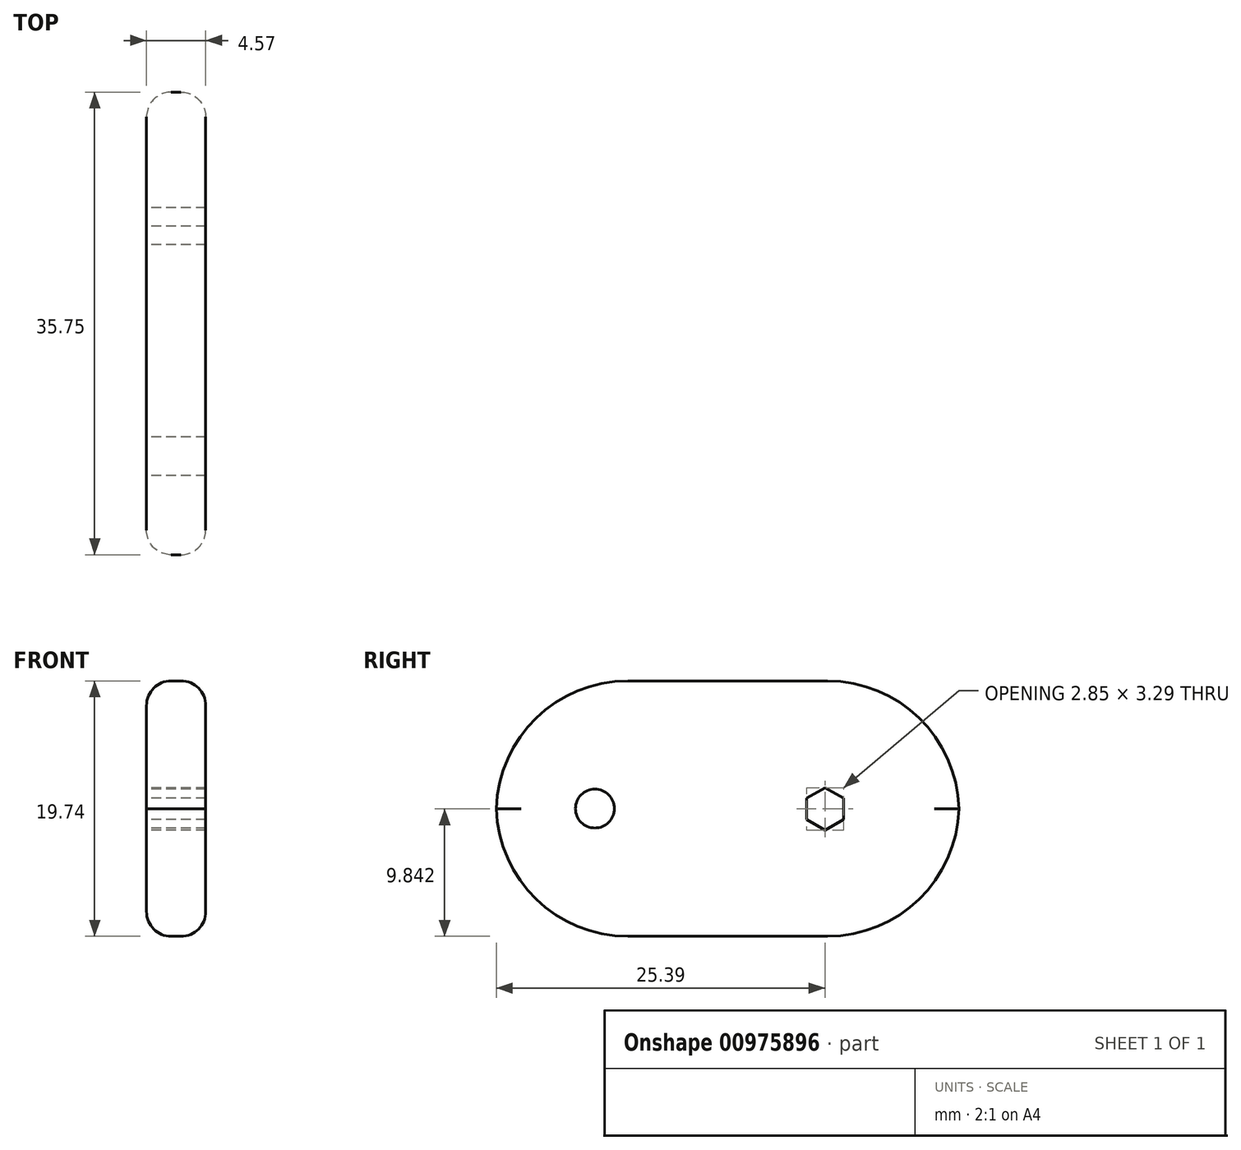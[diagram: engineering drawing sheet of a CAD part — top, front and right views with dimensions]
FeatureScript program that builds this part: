
annotation { "Feature Type Name" : "Feature", "Feature Type Description" : "" }
export const myFeature = defineFeature(function(context is Context, id is Id, definition is map)
    precondition{}
    {
        {
            var Q0;
            Q0=qCreatedBy(makeId("Right.planeOp"),FACE);
            var sketch = newSketch(context, id + "F0", { "sketchPlane" : qUnion([Q0])});
            skCircle(sketch, "E0", {"center": v(0, 0) * mm, "radius": 25.4 * mm});
            skCircle(sketch, "E1", {"center": v(15.88, 0) * mm, "radius": 1.5 * mm});
            skCircle(sketch, "E2", {"center": v(-17.78, 0) * mm, "radius": 1.5 * mm});
            skLineSegment(sketch, "E3.0", {"start": v(1.42, -0.85) * mm, "end": v(0, -1.67) * mm});
            skLineSegment(sketch, "E3.1", {"start": v(0, -1.67) * mm, "end": v(-1.43, -0.85) * mm});
            skLineSegment(sketch, "E3.2", {"start": v(-1.43, -0.85) * mm, "end": v(-1.43, 0.8) * mm});
            skLineSegment(sketch, "E3.3", {"start": v(-1.43, 0.8) * mm, "end": v(0, 1.62) * mm});
            skLineSegment(sketch, "E3.4", {"start": v(0, 1.62) * mm, "end": v(1.43, 0.8) * mm});
            skLineSegment(sketch, "E3.5", {"start": v(1.42, 0.8) * mm, "end": v(1.42, -0.85) * mm});
            skPoint(sketch, "E3.0.midPoint", {"position": v(0.71, -1.26) * mm});
            skLineSegment(sketch, "E4", {"start": v(23.4, 9.87) * mm, "end": v(-23.4, 9.87) * mm});
            skLineSegment(sketch, "E5.MirrorCS", {"start": v(23.4, -9.87) * mm, "end": v(-23.4, -9.87) * mm});
            skLineSegment(sketch, "E6", {"start": v(10.36, 9.87) * mm, "end": v(10.36, -9.87) * mm});
            skSolve(sketch);
        }
        {
            var Q0;
            Q0=makeQuery(id+"F0.imprint","IMPRINT",FACE,{"disambiguationData":[TD([[makeQuery(id+"F0.imprint","IMPRINT",EDGE,{"derivedFrom":sQuery(id+"F0.wireOp",EDGE,"E2")}),-1.0]])]});
            extrude(context, id + "F1", {"entities" : qUnion([Q0]), "depth" : 4.57 * mm, "offsetDistance" : 25.4 * mm});
        }
        {
            var Q0;
            {var subQ0=sQuery(id+"F0.wireOp",EDGE,"E4");var subQ1=sQuery(id+"F0.wireOp",EDGE,"E0");Q0=makeQuery(id+"F1.opExtrude","SWEPT_EDGE",EDGE,{"disambiguationData":[OSD([subQ1,subQ0]),TDD([makeQuery(id+"F0.imprint","INTERSECT",VERTEX,{"disambiguationData":[OD(0.0)],"derivedFrom":[subQ1,subQ0]})])]});}
            var Q1;
            {var subQ0=sQuery(id+"F0.wireOp",EDGE,"E4");var subQ1=sQuery(id+"F0.wireOp",EDGE,"E0");Q1=makeQuery(id+"F1.opExtrude","SWEPT_EDGE",EDGE,{"disambiguationData":[OSD([subQ1,subQ0]),TDD([makeQuery(id+"F0.imprint","INTERSECT",VERTEX,{"disambiguationData":[OD(1.0)],"derivedFrom":[subQ1,subQ0]})])]});}
            var Q2;
            {var subQ0=sQuery(id+"F0.wireOp",EDGE,"E5.MirrorCS");var subQ1=sQuery(id+"F0.wireOp",EDGE,"E0");Q2=makeQuery(id+"F1.opExtrude","SWEPT_EDGE",EDGE,{"disambiguationData":[OSD([subQ1,subQ0]),TDD([makeQuery(id+"F0.imprint","INTERSECT",VERTEX,{"disambiguationData":[OD(1.0)],"derivedFrom":[subQ1,subQ0]})])]});}
            var Q3;
            {var subQ0=sQuery(id+"F0.wireOp",EDGE,"E5.MirrorCS");var subQ1=sQuery(id+"F0.wireOp",EDGE,"E0");Q3=makeQuery(id+"F1.opExtrude","SWEPT_EDGE",EDGE,{"disambiguationData":[OSD([subQ1,subQ0]),TDD([makeQuery(id+"F0.imprint","INTERSECT",VERTEX,{"disambiguationData":[OD(0.0)],"derivedFrom":[subQ1,subQ0]})])]});}
            fillet(context, id + "F2", {"entities" : qUnion([Q0, Q1, Q2, Q3]), "radius" : 10.16 * mm, "tangentPropagation" : true, "allowEdgeOverflow" : false});
        }
        {
            var Q0;
            Q0=makeQuery(id+"F1.opExtrude","SWEPT_EDGE",EDGE,{"disambiguationData":[OSD([sQuery(id+"F0.wireOp",EDGE,"E4"),sQuery(id+"F0.wireOp",EDGE,"E6")])]});
            var Q1;
            Q1=makeQuery(id+"F1.opExtrude","SWEPT_EDGE",EDGE,{"disambiguationData":[OSD([sQuery(id+"F0.wireOp",EDGE,"E5.MirrorCS"),sQuery(id+"F0.wireOp",EDGE,"E6")])]});
            fillet(context, id + "F3", {"entities" : qUnion([Q0, Q1]), "radius" : 10.16 * mm, "tangentPropagation" : true, "allowEdgeOverflow" : false});
        }
        {
            var Q0;
            {var subQ0=sQuery(id+"F0.wireOp",EDGE,"E6");var subQ1=sQuery(id+"F0.wireOp",EDGE,"E4");Q0=makeQuery(id+"F3.opFillet","BLEND_EDGE",EDGE,{"blendedFrom":[makeQuery(id+"F1.opExtrude","SWEPT_EDGE",EDGE,{"disambiguationData":[OSD([subQ1,subQ0])]}),makeQuery(id+"F1.opExtrude","CAP_FACE",FACE,{"disambiguationData":[OSD([sQuery(id+"F0.wireOp",EDGE,"E0"),sQuery(id+"F0.wireOp",EDGE,"E2"),sQuery(id+"F0.wireOp",EDGE,"E3.0"),sQuery(id+"F0.wireOp",EDGE,"E3.1"),sQuery(id+"F0.wireOp",EDGE,"E3.2"),sQuery(id+"F0.wireOp",EDGE,"E3.3"),sQuery(id+"F0.wireOp",EDGE,"E3.4"),sQuery(id+"F0.wireOp",EDGE,"E3.5"),subQ1,sQuery(id+"F0.wireOp",EDGE,"E5.MirrorCS"),subQ0])],"isStart":true})],"blendedInto":[makeQuery(id+"F1.opExtrude","CAP_FACE",FACE,{"disambiguationData":[OSD([sQuery(id+"F0.wireOp",EDGE,"E0"),sQuery(id+"F0.wireOp",EDGE,"E2"),sQuery(id+"F0.wireOp",EDGE,"E3.0"),sQuery(id+"F0.wireOp",EDGE,"E3.1"),sQuery(id+"F0.wireOp",EDGE,"E3.2"),sQuery(id+"F0.wireOp",EDGE,"E3.3"),sQuery(id+"F0.wireOp",EDGE,"E3.4"),sQuery(id+"F0.wireOp",EDGE,"E3.5"),subQ1,sQuery(id+"F0.wireOp",EDGE,"E5.MirrorCS"),subQ0])],"isStart":true})]});}
            var Q1;
            Q1=makeQuery(id+"F1.opExtrude","CAP_EDGE",EDGE,{"disambiguationData":[OSD([sQuery(id+"F0.wireOp",EDGE,"E4")])],"isStart":true});
            var Q2;
            {var subQ0=sQuery(id+"F0.wireOp",EDGE,"E4");var subQ1=sQuery(id+"F0.wireOp",EDGE,"E0");Q2=makeQuery(id+"F2.opFillet","BLEND_EDGE",EDGE,{"blendedFrom":[makeQuery(id+"F1.opExtrude","SWEPT_EDGE",EDGE,{"disambiguationData":[OSD([subQ1,subQ0])]}),makeQuery(id+"F1.opExtrude","CAP_FACE",FACE,{"disambiguationData":[OSD([subQ1,sQuery(id+"F0.wireOp",EDGE,"E2"),sQuery(id+"F0.wireOp",EDGE,"E3.0"),sQuery(id+"F0.wireOp",EDGE,"E3.1"),sQuery(id+"F0.wireOp",EDGE,"E3.2"),sQuery(id+"F0.wireOp",EDGE,"E3.3"),sQuery(id+"F0.wireOp",EDGE,"E3.4"),sQuery(id+"F0.wireOp",EDGE,"E3.5"),subQ0,sQuery(id+"F0.wireOp",EDGE,"E5.MirrorCS"),sQuery(id+"F0.wireOp",EDGE,"E6")])],"isStart":true})],"blendedInto":[makeQuery(id+"F1.opExtrude","CAP_FACE",FACE,{"disambiguationData":[OSD([subQ1,sQuery(id+"F0.wireOp",EDGE,"E2"),sQuery(id+"F0.wireOp",EDGE,"E3.0"),sQuery(id+"F0.wireOp",EDGE,"E3.1"),sQuery(id+"F0.wireOp",EDGE,"E3.2"),sQuery(id+"F0.wireOp",EDGE,"E3.3"),sQuery(id+"F0.wireOp",EDGE,"E3.4"),sQuery(id+"F0.wireOp",EDGE,"E3.5"),subQ0,sQuery(id+"F0.wireOp",EDGE,"E5.MirrorCS"),sQuery(id+"F0.wireOp",EDGE,"E6")])],"isStart":true})]});}
            var Q3;
            {var subQ0=sQuery(id+"F0.wireOp",EDGE,"E5.MirrorCS");var subQ1=sQuery(id+"F0.wireOp",EDGE,"E0");Q3=makeQuery(id+"F2.opFillet","BLEND_EDGE",EDGE,{"blendedFrom":[makeQuery(id+"F1.opExtrude","SWEPT_EDGE",EDGE,{"disambiguationData":[OSD([subQ1,subQ0])]}),makeQuery(id+"F1.opExtrude","CAP_FACE",FACE,{"disambiguationData":[OSD([subQ1,sQuery(id+"F0.wireOp",EDGE,"E2"),sQuery(id+"F0.wireOp",EDGE,"E3.0"),sQuery(id+"F0.wireOp",EDGE,"E3.1"),sQuery(id+"F0.wireOp",EDGE,"E3.2"),sQuery(id+"F0.wireOp",EDGE,"E3.3"),sQuery(id+"F0.wireOp",EDGE,"E3.4"),sQuery(id+"F0.wireOp",EDGE,"E3.5"),sQuery(id+"F0.wireOp",EDGE,"E4"),subQ0,sQuery(id+"F0.wireOp",EDGE,"E6")])],"isStart":true})],"blendedInto":[makeQuery(id+"F1.opExtrude","CAP_FACE",FACE,{"disambiguationData":[OSD([subQ1,sQuery(id+"F0.wireOp",EDGE,"E2"),sQuery(id+"F0.wireOp",EDGE,"E3.0"),sQuery(id+"F0.wireOp",EDGE,"E3.1"),sQuery(id+"F0.wireOp",EDGE,"E3.2"),sQuery(id+"F0.wireOp",EDGE,"E3.3"),sQuery(id+"F0.wireOp",EDGE,"E3.4"),sQuery(id+"F0.wireOp",EDGE,"E3.5"),sQuery(id+"F0.wireOp",EDGE,"E4"),subQ0,sQuery(id+"F0.wireOp",EDGE,"E6")])],"isStart":true})]});}
            var Q4;
            Q4=makeQuery(id+"F1.opExtrude","CAP_EDGE",EDGE,{"disambiguationData":[OSD([sQuery(id+"F0.wireOp",EDGE,"E5.MirrorCS")])],"isStart":true});
            var Q5;
            {var subQ0=sQuery(id+"F0.wireOp",EDGE,"E6");var subQ1=sQuery(id+"F0.wireOp",EDGE,"E5.MirrorCS");Q5=makeQuery(id+"F3.opFillet","BLEND_EDGE",EDGE,{"blendedFrom":[makeQuery(id+"F1.opExtrude","SWEPT_EDGE",EDGE,{"disambiguationData":[OSD([subQ1,subQ0])]}),makeQuery(id+"F1.opExtrude","CAP_FACE",FACE,{"disambiguationData":[OSD([sQuery(id+"F0.wireOp",EDGE,"E0"),sQuery(id+"F0.wireOp",EDGE,"E2"),sQuery(id+"F0.wireOp",EDGE,"E3.0"),sQuery(id+"F0.wireOp",EDGE,"E3.1"),sQuery(id+"F0.wireOp",EDGE,"E3.2"),sQuery(id+"F0.wireOp",EDGE,"E3.3"),sQuery(id+"F0.wireOp",EDGE,"E3.4"),sQuery(id+"F0.wireOp",EDGE,"E3.5"),sQuery(id+"F0.wireOp",EDGE,"E4"),subQ1,subQ0])],"isStart":true})],"blendedInto":[makeQuery(id+"F1.opExtrude","CAP_FACE",FACE,{"disambiguationData":[OSD([sQuery(id+"F0.wireOp",EDGE,"E0"),sQuery(id+"F0.wireOp",EDGE,"E2"),sQuery(id+"F0.wireOp",EDGE,"E3.0"),sQuery(id+"F0.wireOp",EDGE,"E3.1"),sQuery(id+"F0.wireOp",EDGE,"E3.2"),sQuery(id+"F0.wireOp",EDGE,"E3.3"),sQuery(id+"F0.wireOp",EDGE,"E3.4"),sQuery(id+"F0.wireOp",EDGE,"E3.5"),sQuery(id+"F0.wireOp",EDGE,"E4"),subQ1,subQ0])],"isStart":true})]});}
            var Q6;
            {var subQ0=sQuery(id+"F0.wireOp",EDGE,"E4");var subQ1=sQuery(id+"F0.wireOp",EDGE,"E0");Q6=makeQuery(id+"F2.opFillet","BLEND_EDGE",EDGE,{"blendedFrom":[makeQuery(id+"F1.opExtrude","SWEPT_EDGE",EDGE,{"disambiguationData":[OSD([subQ1,subQ0])]}),makeQuery(id+"F1.opExtrude","CAP_FACE",FACE,{"disambiguationData":[OSD([subQ1,sQuery(id+"F0.wireOp",EDGE,"E2"),sQuery(id+"F0.wireOp",EDGE,"E3.0"),sQuery(id+"F0.wireOp",EDGE,"E3.1"),sQuery(id+"F0.wireOp",EDGE,"E3.2"),sQuery(id+"F0.wireOp",EDGE,"E3.3"),sQuery(id+"F0.wireOp",EDGE,"E3.4"),sQuery(id+"F0.wireOp",EDGE,"E3.5"),subQ0,sQuery(id+"F0.wireOp",EDGE,"E5.MirrorCS"),sQuery(id+"F0.wireOp",EDGE,"E6")])],"isStart":false})],"blendedInto":[makeQuery(id+"F1.opExtrude","CAP_FACE",FACE,{"disambiguationData":[OSD([subQ1,sQuery(id+"F0.wireOp",EDGE,"E2"),sQuery(id+"F0.wireOp",EDGE,"E3.0"),sQuery(id+"F0.wireOp",EDGE,"E3.1"),sQuery(id+"F0.wireOp",EDGE,"E3.2"),sQuery(id+"F0.wireOp",EDGE,"E3.3"),sQuery(id+"F0.wireOp",EDGE,"E3.4"),sQuery(id+"F0.wireOp",EDGE,"E3.5"),subQ0,sQuery(id+"F0.wireOp",EDGE,"E5.MirrorCS"),sQuery(id+"F0.wireOp",EDGE,"E6")])],"isStart":false})]});}
            var Q7;
            Q7=makeQuery(id+"F1.opExtrude","CAP_EDGE",EDGE,{"disambiguationData":[OSD([sQuery(id+"F0.wireOp",EDGE,"E4")])],"isStart":false});
            var Q8;
            {var subQ0=sQuery(id+"F0.wireOp",EDGE,"E6");var subQ1=sQuery(id+"F0.wireOp",EDGE,"E4");Q8=makeQuery(id+"F3.opFillet","BLEND_EDGE",EDGE,{"blendedFrom":[makeQuery(id+"F1.opExtrude","SWEPT_EDGE",EDGE,{"disambiguationData":[OSD([subQ1,subQ0])]}),makeQuery(id+"F1.opExtrude","CAP_FACE",FACE,{"disambiguationData":[OSD([sQuery(id+"F0.wireOp",EDGE,"E0"),sQuery(id+"F0.wireOp",EDGE,"E2"),sQuery(id+"F0.wireOp",EDGE,"E3.0"),sQuery(id+"F0.wireOp",EDGE,"E3.1"),sQuery(id+"F0.wireOp",EDGE,"E3.2"),sQuery(id+"F0.wireOp",EDGE,"E3.3"),sQuery(id+"F0.wireOp",EDGE,"E3.4"),sQuery(id+"F0.wireOp",EDGE,"E3.5"),subQ1,sQuery(id+"F0.wireOp",EDGE,"E5.MirrorCS"),subQ0])],"isStart":false})],"blendedInto":[makeQuery(id+"F1.opExtrude","CAP_FACE",FACE,{"disambiguationData":[OSD([sQuery(id+"F0.wireOp",EDGE,"E0"),sQuery(id+"F0.wireOp",EDGE,"E2"),sQuery(id+"F0.wireOp",EDGE,"E3.0"),sQuery(id+"F0.wireOp",EDGE,"E3.1"),sQuery(id+"F0.wireOp",EDGE,"E3.2"),sQuery(id+"F0.wireOp",EDGE,"E3.3"),sQuery(id+"F0.wireOp",EDGE,"E3.4"),sQuery(id+"F0.wireOp",EDGE,"E3.5"),subQ1,sQuery(id+"F0.wireOp",EDGE,"E5.MirrorCS"),subQ0])],"isStart":false})]});}
            var Q9;
            {var subQ0=sQuery(id+"F0.wireOp",EDGE,"E6");var subQ1=sQuery(id+"F0.wireOp",EDGE,"E5.MirrorCS");Q9=makeQuery(id+"F3.opFillet","BLEND_EDGE",EDGE,{"blendedFrom":[makeQuery(id+"F1.opExtrude","SWEPT_EDGE",EDGE,{"disambiguationData":[OSD([subQ1,subQ0])]}),makeQuery(id+"F1.opExtrude","CAP_FACE",FACE,{"disambiguationData":[OSD([sQuery(id+"F0.wireOp",EDGE,"E0"),sQuery(id+"F0.wireOp",EDGE,"E2"),sQuery(id+"F0.wireOp",EDGE,"E3.0"),sQuery(id+"F0.wireOp",EDGE,"E3.1"),sQuery(id+"F0.wireOp",EDGE,"E3.2"),sQuery(id+"F0.wireOp",EDGE,"E3.3"),sQuery(id+"F0.wireOp",EDGE,"E3.4"),sQuery(id+"F0.wireOp",EDGE,"E3.5"),sQuery(id+"F0.wireOp",EDGE,"E4"),subQ1,subQ0])],"isStart":false})],"blendedInto":[makeQuery(id+"F1.opExtrude","CAP_FACE",FACE,{"disambiguationData":[OSD([sQuery(id+"F0.wireOp",EDGE,"E0"),sQuery(id+"F0.wireOp",EDGE,"E2"),sQuery(id+"F0.wireOp",EDGE,"E3.0"),sQuery(id+"F0.wireOp",EDGE,"E3.1"),sQuery(id+"F0.wireOp",EDGE,"E3.2"),sQuery(id+"F0.wireOp",EDGE,"E3.3"),sQuery(id+"F0.wireOp",EDGE,"E3.4"),sQuery(id+"F0.wireOp",EDGE,"E3.5"),sQuery(id+"F0.wireOp",EDGE,"E4"),subQ1,subQ0])],"isStart":false})]});}
            var Q10;
            Q10=makeQuery(id+"F1.opExtrude","CAP_EDGE",EDGE,{"disambiguationData":[OSD([sQuery(id+"F0.wireOp",EDGE,"E5.MirrorCS")])],"isStart":false});
            var Q11;
            {var subQ0=sQuery(id+"F0.wireOp",EDGE,"E5.MirrorCS");var subQ1=sQuery(id+"F0.wireOp",EDGE,"E0");Q11=makeQuery(id+"F2.opFillet","BLEND_EDGE",EDGE,{"blendedFrom":[makeQuery(id+"F1.opExtrude","SWEPT_EDGE",EDGE,{"disambiguationData":[OSD([subQ1,subQ0])]}),makeQuery(id+"F1.opExtrude","CAP_FACE",FACE,{"disambiguationData":[OSD([subQ1,sQuery(id+"F0.wireOp",EDGE,"E2"),sQuery(id+"F0.wireOp",EDGE,"E3.0"),sQuery(id+"F0.wireOp",EDGE,"E3.1"),sQuery(id+"F0.wireOp",EDGE,"E3.2"),sQuery(id+"F0.wireOp",EDGE,"E3.3"),sQuery(id+"F0.wireOp",EDGE,"E3.4"),sQuery(id+"F0.wireOp",EDGE,"E3.5"),sQuery(id+"F0.wireOp",EDGE,"E4"),subQ0,sQuery(id+"F0.wireOp",EDGE,"E6")])],"isStart":false})],"blendedInto":[makeQuery(id+"F1.opExtrude","CAP_FACE",FACE,{"disambiguationData":[OSD([subQ1,sQuery(id+"F0.wireOp",EDGE,"E2"),sQuery(id+"F0.wireOp",EDGE,"E3.0"),sQuery(id+"F0.wireOp",EDGE,"E3.1"),sQuery(id+"F0.wireOp",EDGE,"E3.2"),sQuery(id+"F0.wireOp",EDGE,"E3.3"),sQuery(id+"F0.wireOp",EDGE,"E3.4"),sQuery(id+"F0.wireOp",EDGE,"E3.5"),sQuery(id+"F0.wireOp",EDGE,"E4"),subQ0,sQuery(id+"F0.wireOp",EDGE,"E6")])],"isStart":false})]});}
            fillet(context, id + "F4", {"entities" : qUnion([Q0, Q1, Q2, Q3, Q4, Q5, Q6, Q7, Q8, Q9, Q10, Q11]), "radius" : 1.9 * mm, "tangentPropagation" : true, "allowEdgeOverflow" : false});
        }
    });
